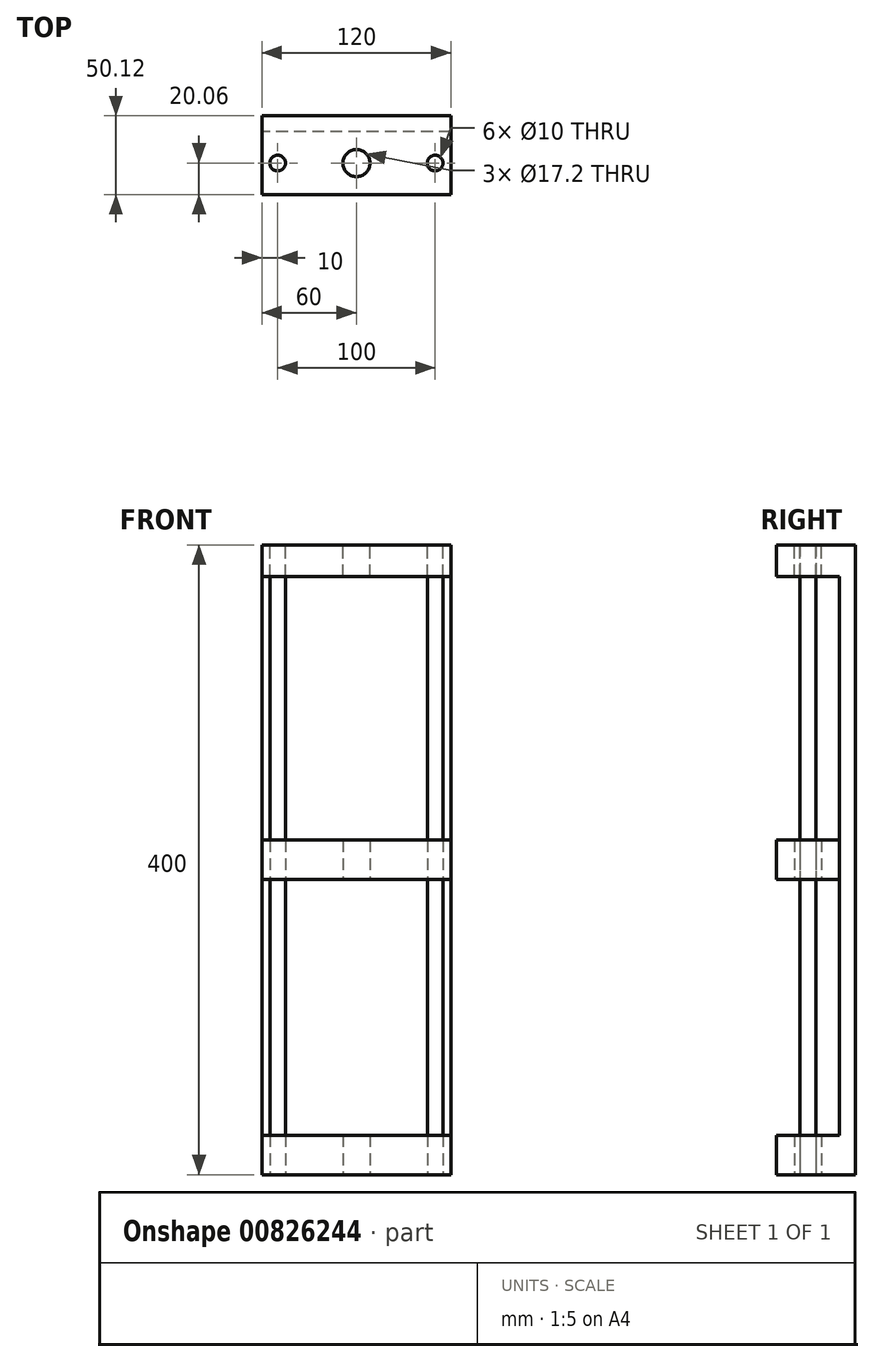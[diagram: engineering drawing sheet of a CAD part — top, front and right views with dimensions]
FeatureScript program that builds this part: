
annotation { "Feature Type Name" : "Feature", "Feature Type Description" : "" }
export const myFeature = defineFeature(function(context is Context, id is Id, definition is map)
    precondition{}
    {
        {
            var Q0;
            Q0=qCreatedBy(makeId("Top.planeOp"),FACE);
            var sketch = newSketch(context, id + "F0", { "sketchPlane" : qUnion([Q0])});
            skLineSegment(sketch, "E0.bottom", {"start": v(-60, 20.06) * mm, "end": v(60, 20.06) * mm});
            skLineSegment(sketch, "E0.top", {"start": v(-60, -20.06) * mm, "end": v(60, -20.06) * mm});
            skLineSegment(sketch, "E0.left", {"start": v(-60, 20.06) * mm, "end": v(-60, -20.06) * mm});
            skLineSegment(sketch, "E0.right", {"start": v(60, 20.06) * mm, "end": v(60, -20.06) * mm});
            skLineSegment(sketch, "E1", {"start": v(0, 0) * mm, "end": v(-60, 0) * mm, "construction": true});
            skLineSegment(sketch, "E2", {"start": v(0, 0) * mm, "end": v(0, 20.06) * mm, "construction": true});
            skCircle(sketch, "E3", {"center": v(-50, 0) * mm, "radius": 5 * mm});
            skCircle(sketch, "E4", {"center": v(50, 0) * mm, "radius": 5 * mm});
            skLineSegment(sketch, "E5", {"start": v(0, 0) * mm, "end": v(50, 0) * mm});
            skCircle(sketch, "E6", {"center": v(0, 0) * mm, "radius": 8.6 * mm});
            skSolve(sketch);
        }
        {
            var Q0;
            Q0=makeQuery(id+"F0.imprint","IMPRINT",FACE,{"disambiguationData":[TD([[makeQuery(id+"F0.imprint","IMPRINT",EDGE,{"derivedFrom":sQuery(id+"F0.wireOp",EDGE,"E3")}),1.0]])]});
            var Q1;
            {var subQ0=sQuery(id+"F0.wireOp",EDGE,"E4");var subQ1=makeQuery(id+"F0.imprint","IMPRINT",VERTEX,{"disambiguationData":[OD(0.0)],"derivedFrom":subQ0});Q1=makeQuery(id+"F0.imprint","IMPRINT",FACE,{"disambiguationData":[TD([[makeQuery(id+"F0.imprint","IMPRINT",EDGE,{"disambiguationData":[TD([[subQ1,1.0]])],"derivedFrom":subQ0}),1.0]])]});}
            extrude(context, id + "F1", {"entities" : qUnion([Q0, Q1]), "endBound" : BoundingType.SYMMETRIC, "depth" : 400 * mm, "offsetDistance" : 25 * mm});
        }
        {
            var Q0;
            Q0=makeQuery(id+"F1.opExtrude","CAP_FACE",FACE,{"disambiguationData":[OSD([sQuery(id+"F0.wireOp",EDGE,"E3")])],"isStart":false});
            var sketch = newSketch(context, id + "F2", { "sketchPlane" : qUnion([Q0])});
            skLineSegment(sketch, "E7.0.0", {"start": v(60, 20.06) * mm, "end": v(-60, 20.06) * mm});
            skLineSegment(sketch, "E7.0.1", {"start": v(-60, 20.06) * mm, "end": v(-60, -20.06) * mm});
            skLineSegment(sketch, "E7.0.2", {"start": v(-60, -20.06) * mm, "end": v(60, -20.06) * mm});
            skLineSegment(sketch, "E7.0.3", {"start": v(60, -20.06) * mm, "end": v(60, 20.06) * mm});
            skCircle(sketch, "E8.0", {"center": v(-50, 0) * mm, "radius": 5 * mm});
            skCircle(sketch, "E9.0", {"center": v(50, 0) * mm, "radius": 5 * mm});
            skCircle(sketch, "E10.0", {"center": v(0, 0) * mm, "radius": 8.6 * mm});
            skSolve(sketch);
        }
        {
            var Q0;
            Q0=makeQuery(id+"F1.opExtrude","CAP_FACE",FACE,{"disambiguationData":[OSD([sQuery(id+"F0.wireOp",EDGE,"E3")])],"isStart":true});
            var sketch = newSketch(context, id + "F3", { "sketchPlane" : qUnion([Q0])});
            skLineSegment(sketch, "E11.0.0", {"start": v(60, -20.06) * mm, "end": v(-60, -20.06) * mm});
            skLineSegment(sketch, "E11.0.1", {"start": v(-60, -20.06) * mm, "end": v(-60, 20.06) * mm});
            skLineSegment(sketch, "E11.0.2", {"start": v(-60, 20.06) * mm, "end": v(60, 20.06) * mm});
            skLineSegment(sketch, "E11.0.3", {"start": v(60, 20.06) * mm, "end": v(60, -20.06) * mm});
            skCircle(sketch, "E12.0", {"center": v(-50, 0) * mm, "radius": 5 * mm});
            skCircle(sketch, "E12.1", {"center": v(50, 0) * mm, "radius": 5 * mm});
            skCircle(sketch, "E12.2", {"center": v(0, 0) * mm, "radius": 8.6 * mm});
            skSolve(sketch);
        }
        {
            var Q0;
            Q0=makeQuery(id+"F2.imprint","IMPRINT",FACE,{"disambiguationData":[TD([[makeQuery(id+"F2.imprint","IMPRINT",EDGE,{"derivedFrom":sQuery(id+"F2.wireOp",EDGE,"E7.0.0")}),1.0]])]});
            extrude(context, id + "F4", {"entities" : qUnion([Q0]), "oppositeDirection" : true, "depth" : 20 * mm, "offsetDistance" : 25 * mm});
        }
        {
            var Q0;
            Q0=makeQuery(id+"F3.imprint","IMPRINT",FACE,{"disambiguationData":[TD([[makeQuery(id+"F3.imprint","IMPRINT",EDGE,{"derivedFrom":sQuery(id+"F3.wireOp",EDGE,"E11.0.0")}),-1.0]])]});
            extrude(context, id + "F5", {"entities" : qUnion([Q0]), "oppositeDirection" : true, "depth" : 25 * mm, "offsetDistance" : 25 * mm});
        }
        {
            var Q0;
            Q0=makeQuery(id+"F4.opExtrude","SWEPT_FACE",FACE,{"disambiguationData":[OSD([sQuery(id+"F2.wireOp",EDGE,"E7.0.0")])]});
            var sketch = newSketch(context, id + "F6", { "sketchPlane" : qUnion([Q0])});
            skLineSegment(sketch, "E13.1", {"start": v(-60, 200) * mm, "end": v(60, 200) * mm});
            skLineSegment(sketch, "E13.2", {"start": v(60, 180) * mm, "end": v(60, 200) * mm});
            skLineSegment(sketch, "E13.3", {"start": v(-60, 180) * mm, "end": v(60, 180) * mm});
            skLineSegment(sketch, "E13.4", {"start": v(-60, 180) * mm, "end": v(-60, 200) * mm});
            skLineSegment(sketch, "E14.0", {"start": v(60, -175) * mm, "end": v(60, -200) * mm});
            skLineSegment(sketch, "E14.1", {"start": v(-60, -200) * mm, "end": v(60, -200) * mm});
            skLineSegment(sketch, "E14.2", {"start": v(-60, -175) * mm, "end": v(-60, -200) * mm});
            skLineSegment(sketch, "E14.3", {"start": v(-60, -175) * mm, "end": v(60, -175) * mm});
            skSolve(sketch);
        }
        {
            var Q0;
            Q0=makeQuery(id+"F6.imprint","IMPRINT",FACE,{"disambiguationData":[TD([[makeQuery(id+"F6.imprint","IMPRINT",EDGE,{"derivedFrom":sQuery(id+"F6.wireOp",EDGE,"E14.0")}),-1.0]])]});
            var Q1;
            Q1=makeQuery(id+"F6.imprint","IMPRINT",FACE,{"disambiguationData":[TD([[makeQuery(id+"F6.imprint","IMPRINT",EDGE,{"derivedFrom":sQuery(id+"F6.wireOp",EDGE,"E13.1")}),-1.0]])]});
            extrude(context, id + "F7", {"entities" : qUnion([Q0, Q1]), "depth" : 10 * mm, "offsetDistance" : 25 * mm});
        }
        {
            var Q0;
            Q0=makeQuery(id+"F7.opExtrude","SWEPT_FACE",FACE,{"disambiguationData":[OSD([sQuery(id+"F6.wireOp",EDGE,"E14.3")])]});
            extrude(context, id + "F8", {"entities" : qUnion([Q0]), "operationType" : NewBodyOperationType.ADD, "endBound" : BoundingType.UP_TO_NEXT, "depth" : 25 * mm, "offsetDistance" : 25 * mm});
        }
        {
            var Q0;
            Q0=makeQuery(id+"F0.imprint","IMPRINT",FACE,{"disambiguationData":[TD([[makeQuery(id+"F0.imprint","IMPRINT",EDGE,{"derivedFrom":sQuery(id+"F0.wireOp",EDGE,"E0.bottom")}),-1.0]])]});
            extrude(context, id + "F9", {"entities" : qUnion([Q0]), "endBound" : BoundingType.SYMMETRIC, "depth" : 25 * mm, "offsetDistance" : 25 * mm});
        }
    });
